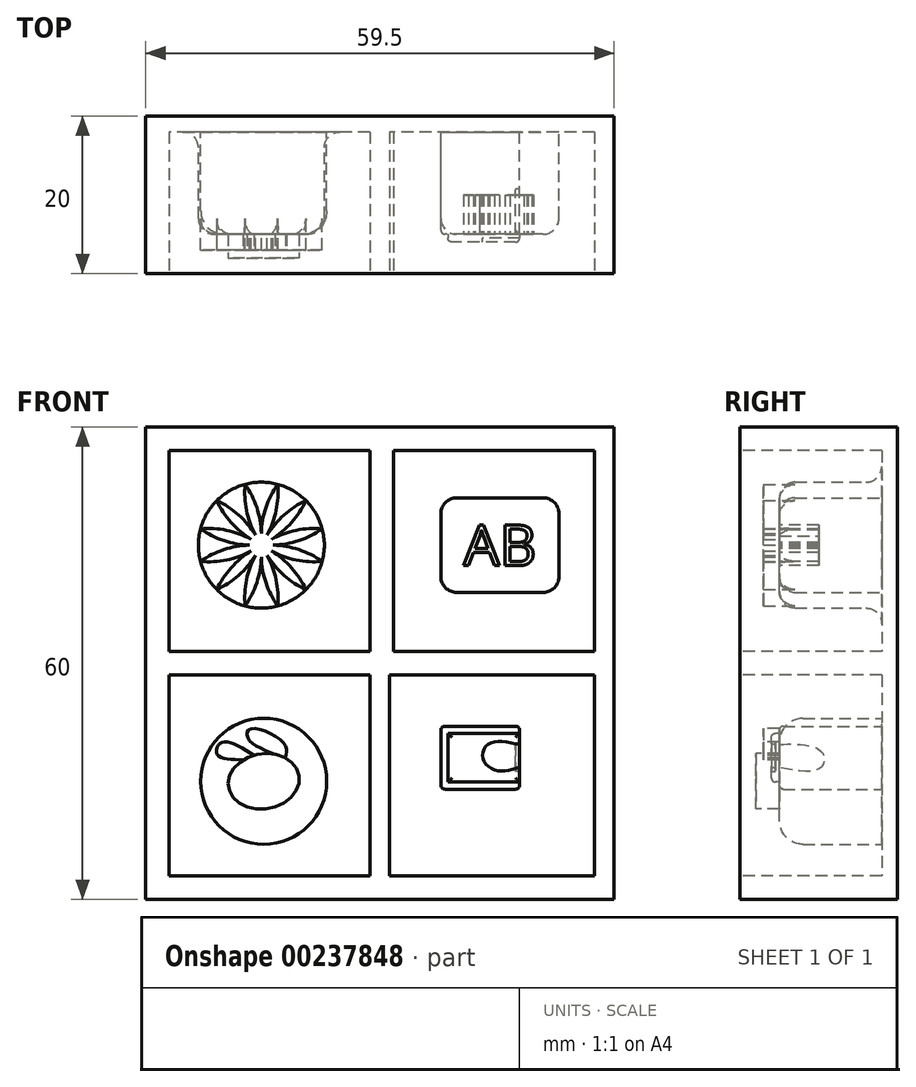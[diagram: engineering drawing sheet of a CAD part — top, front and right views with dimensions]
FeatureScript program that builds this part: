
annotation { "Feature Type Name" : "Feature", "Feature Type Description" : "" }
export const myFeature = defineFeature(function(context is Context, id is Id, definition is map)
    precondition{}
    {
        {
            var Q0;
            Q0=qCreatedBy(makeId("Front.planeOp"),FACE);
            var sketch = newSketch(context, id + "F0", { "sketchPlane" : qUnion([Q0])});
            skLineSegment(sketch, "E0.bottom", {"start": v(30, -30) * mm, "end": v(-30, -30) * mm});
            skLineSegment(sketch, "E0.top", {"start": v(30, 30) * mm, "end": v(-30, 30) * mm});
            skLineSegment(sketch, "E0.left", {"start": v(30, -30) * mm, "end": v(30, 30) * mm});
            skLineSegment(sketch, "E0.right", {"start": v(-30, -30) * mm, "end": v(-30, 30) * mm});
            skPoint(sketch, "E0.middle", {"position": v(0, 0) * mm});
            skSolve(sketch);
        }
        {
            var Q0;
            Q0 = qSketchRegion(id + "F2", true);
            var Q1;
            Q1=makeQuery(id+"F0.imprint","IMPRINT",FACE,{"disambiguationData":[TD([[makeQuery(id+"F0.imprint","IMPRINT",EDGE,{"derivedFrom":sQuery(id+"F0.wireOp",EDGE,"E0.bottom")}),-1.0]])]});
            var Q2;
            Q2 = qSketchRegion(id + "F6", true);
            extrude(context, id + "F1", {"entities" : qUnion([Q0, Q1, Q2]), "depth" : 20 * mm});
        }
        {
            var Q0;
            Q0=makeQuery(id+"F1.opExtrude","CAP_FACE",FACE,{"disambiguationData":[OSD([sQuery(id+"F0.wireOp",EDGE,"E0.bottom"),sQuery(id+"F0.wireOp",EDGE,"E0.top"),sQuery(id+"F0.wireOp",EDGE,"E0.left"),sQuery(id+"F0.wireOp",EDGE,"E0.right")])],"isStart":false});
            var sketch = newSketch(context, id + "F2", { "sketchPlane" : qUnion([Q0])});
            skLineSegment(sketch, "E1.bottom", {"start": v(27, 27) * mm, "end": v(-27, 27) * mm});
            skLineSegment(sketch, "E1.top", {"start": v(27, -27) * mm, "end": v(-27, -27) * mm});
            skLineSegment(sketch, "E1.left", {"start": v(27, 27) * mm, "end": v(27, -27) * mm});
            skLineSegment(sketch, "E1.right", {"start": v(-27, 27) * mm, "end": v(-27, -27) * mm});
            skPoint(sketch, "E1.middle", {"position": v(0, 0) * mm});
            skLineSegment(sketch, "E2.bottom", {"start": v(1.5, 27) * mm, "end": v(-1.5, 27) * mm});
            skLineSegment(sketch, "E2.top", {"start": v(1.5, -27) * mm, "end": v(-1.5, -27) * mm});
            skLineSegment(sketch, "E2.left", {"start": v(1.5, 27) * mm, "end": v(1.5, -27) * mm});
            skLineSegment(sketch, "E2.right", {"start": v(-1.5, 27) * mm, "end": v(-1.5, -27) * mm});
            skLineSegment(sketch, "E3.bottom", {"start": v(-27, 1.5) * mm, "end": v(27, 1.5) * mm});
            skLineSegment(sketch, "E3.top", {"start": v(-27, -1.5) * mm, "end": v(27, -1.5) * mm});
            skLineSegment(sketch, "E3.left", {"start": v(-27, 1.5) * mm, "end": v(-27, -1.5) * mm});
            skLineSegment(sketch, "E3.right", {"start": v(27, 1.5) * mm, "end": v(27, -1.5) * mm});
            skSolve(sketch);
        }
        {
            var Q0;
            {var subQ0=sQuery(id+"F2.wireOp",EDGE,"E1.right");var subQ1=sQuery(id+"F2.wireOp",EDGE,"E1.top");var subQ2=makeQuery(id+"F2.imprint","INTERSECT",VERTEX,{"derivedFrom":[subQ1,subQ0]});Q0=makeQuery(id+"F2.imprint","IMPRINT",FACE,{"disambiguationData":[TD([[makeQuery(id+"F2.imprint","IMPRINT",EDGE,{"disambiguationData":[TD([[subQ2,1.0]])],"derivedFrom":subQ1}),-1.0]])]});}
            extrude(context, id + "F3", {"entities" : qUnion([Q0]), "operationType" : NewBodyOperationType.REMOVE, "oppositeDirection" : true, "depth" : 18 * mm});
        }
        {
            var Q0;
            {var subQ0=sQuery(id+"F2.wireOp",EDGE,"E1.right");var subQ1=sQuery(id+"F2.wireOp",EDGE,"E1.bottom");var subQ2=makeQuery(id+"F2.imprint","INTERSECT",VERTEX,{"derivedFrom":[subQ1,subQ0]});Q0=makeQuery(id+"F2.imprint","IMPRINT",FACE,{"disambiguationData":[TD([[makeQuery(id+"F2.imprint","IMPRINT",EDGE,{"disambiguationData":[TD([[subQ2,1.0]])],"derivedFrom":subQ1}),1.0]])]});}
            extrude(context, id + "F4", {"entities" : qUnion([Q0]), "operationType" : NewBodyOperationType.REMOVE, "oppositeDirection" : true, "depth" : 18 * mm});
        }
        {
            var Q0;
            {var subQ0=sQuery(id+"F2.wireOp",EDGE,"E1.left");var subQ1=sQuery(id+"F2.wireOp",EDGE,"E1.top");var subQ2=makeQuery(id+"F2.imprint","INTERSECT",VERTEX,{"derivedFrom":[subQ1,subQ0]});Q0=makeQuery(id+"F2.imprint","IMPRINT",FACE,{"disambiguationData":[TD([[makeQuery(id+"F2.imprint","IMPRINT",EDGE,{"disambiguationData":[TD([[subQ2,-1.0]])],"derivedFrom":subQ1}),-1.0]])]});}
            var Q1;
            {var subQ0=sQuery(id+"F2.wireOp",EDGE,"E1.left");var subQ1=sQuery(id+"F2.wireOp",EDGE,"E1.bottom");var subQ2=makeQuery(id+"F2.imprint","INTERSECT",VERTEX,{"derivedFrom":[subQ1,subQ0]});Q1=makeQuery(id+"F2.imprint","IMPRINT",FACE,{"disambiguationData":[TD([[makeQuery(id+"F2.imprint","IMPRINT",EDGE,{"disambiguationData":[TD([[subQ2,-1.0]])],"derivedFrom":subQ1}),1.0]])]});}
            extrude(context, id + "F5", {"entities" : qUnion([Q0, Q1]), "operationType" : NewBodyOperationType.REMOVE, "oppositeDirection" : true, "depth" : 18 * mm});
        }
        {
            var Q0;
            Q0=qCreatedBy(makeId("Front.planeOp"),FACE);
            var sketch = newSketch(context, id + "F6", { "sketchPlane" : qUnion([Q0])});
            skCircle(sketch, "E4", {"center": v(-15.3, 15) * mm, "radius": 8 * mm});
            skCircle(sketch, "E5", {"center": v(-15, -15) * mm, "radius": 8 * mm});
            skLineSegment(sketch, "E6.bottom", {"start": v(22.5, 9) * mm, "end": v(7.5, 9) * mm});
            skLineSegment(sketch, "E6.top", {"start": v(22.5, 21) * mm, "end": v(7.5, 21) * mm});
            skLineSegment(sketch, "E6.left", {"start": v(22.5, 9) * mm, "end": v(22.5, 21) * mm});
            skLineSegment(sketch, "E6.right", {"start": v(7.5, 9) * mm, "end": v(7.5, 21) * mm});
            skPoint(sketch, "E6.middle", {"position": v(15, 15) * mm});
            skLineSegment(sketch, "E7.bottom", {"start": v(17.5, -16) * mm, "end": v(7.5, -16) * mm});
            skLineSegment(sketch, "E7.top", {"start": v(17.5, -8) * mm, "end": v(7.5, -8) * mm});
            skLineSegment(sketch, "E7.left", {"start": v(17.5, -16) * mm, "end": v(17.5, -8) * mm});
            skLineSegment(sketch, "E7.right", {"start": v(7.5, -16) * mm, "end": v(7.5, -8) * mm});
            skPoint(sketch, "E7.middle", {"position": v(12.5, -12) * mm});
            skSolve(sketch);
        }
        {
            var Q0;
            Q0=makeQuery(id+"F6.imprint","IMPRINT",FACE,{"disambiguationData":[TD([[makeQuery(id+"F6.imprint","IMPRINT",EDGE,{"derivedFrom":sQuery(id+"F6.wireOp",EDGE,"E4")}),1.0]])]});
            var Q1;
            Q1=makeQuery(id+"F6.imprint","IMPRINT",FACE,{"disambiguationData":[TD([[makeQuery(id+"F6.imprint","IMPRINT",EDGE,{"derivedFrom":sQuery(id+"F6.wireOp",EDGE,"E6.bottom")}),-1.0]])]});
            var Q2;
            Q2=makeQuery(id+"F6.imprint","IMPRINT",FACE,{"disambiguationData":[TD([[makeQuery(id+"F6.imprint","IMPRINT",EDGE,{"derivedFrom":sQuery(id+"F6.wireOp",EDGE,"E7.bottom")}),-1.0]])]});
            extrude(context, id + "F7", {"entities" : qUnion([Q0, Q1, Q2]), "operationType" : NewBodyOperationType.ADD, "depth" : 15 * mm});
        }
        {
            var Q0;
            Q0=makeQuery(id+"F6.imprint","IMPRINT",FACE,{"disambiguationData":[TD([[makeQuery(id+"F6.imprint","IMPRINT",EDGE,{"derivedFrom":sQuery(id+"F6.wireOp",EDGE,"E5")}),1.0]])]});
            var Q1;
            Q1=sQuery(id+"F6.wireOp",EDGE,"E5");
            extrude(context, id + "F8", {"entities" : qUnion([Q0]), "operationType" : NewBodyOperationType.ADD, "surfaceEntities" : qUnion([Q1]), "depth" : 15 * mm});
        }
        {
            var Q0;
            Q0=qCreatedBy(makeId("Front.planeOp"),FACE);
            var sketch = newSketch(context, id + "F9", { "sketchPlane" : qUnion([Q0])});
            skCircle(sketch, "E8", {"center": v(-15.3, 15) * mm, "radius": 1.5 * mm});
            skArc(sketch, "E9", {"start": v(-13.24, 7.27) * mm, "mid": v(-13.42, 10.58) * mm, "end": v(-14.56, 13.7) * mm});
            skArc(sketch, "E10.MirrorCS", {"start": v(-13.24, 7.27) * mm, "mid": v(-14.73, 10.23) * mm, "end": v(-15.3, 13.5) * mm});
            skArc(sketch, "E11.MirrorCS", {"start": v(-9.65, 9.34) * mm, "mid": v(-12.42, 11.16) * mm, "end": v(-14.56, 13.7) * mm});
            skArc(sketch, "E12.MirrorCS", {"start": v(-9.65, 9.34) * mm, "mid": v(-11.47, 12.12) * mm, "end": v(-14, 14.25) * mm});
            skArc(sketch, "E13.MirrorCS", {"start": v(-7.58, 12.93) * mm, "mid": v(-10.9, 13.11) * mm, "end": v(-14, 14.25) * mm});
            skArc(sketch, "E14.MirrorCS", {"start": v(-7.58, 12.93) * mm, "mid": v(-10.54, 14.43) * mm, "end": v(-13.8, 15) * mm});
            skArc(sketch, "E15.MirrorCS", {"start": v(-7.58, 17.07) * mm, "mid": v(-10.54, 15.57) * mm, "end": v(-13.8, 15) * mm});
            skArc(sketch, "E16.MirrorCS", {"start": v(-7.58, 17.07) * mm, "mid": v(-10.9, 16.89) * mm, "end": v(-14, 15.75) * mm});
            skArc(sketch, "E17.MirrorCS", {"start": v(-9.65, 20.66) * mm, "mid": v(-11.47, 17.88) * mm, "end": v(-14, 15.75) * mm});
            skArc(sketch, "E18.MirrorCS", {"start": v(-9.65, 20.66) * mm, "mid": v(-12.42, 18.84) * mm, "end": v(-14.56, 16.3) * mm});
            skArc(sketch, "E19.MirrorCS", {"start": v(-13.24, 22.73) * mm, "mid": v(-13.42, 19.42) * mm, "end": v(-14.56, 16.3) * mm});
            skArc(sketch, "E20.MirrorCS", {"start": v(-13.24, 22.73) * mm, "mid": v(-14.73, 19.77) * mm, "end": v(-15.3, 16.5) * mm});
            skArc(sketch, "E21.MirrorCS", {"start": v(-17.38, 22.73) * mm, "mid": v(-15.88, 19.77) * mm, "end": v(-15.3, 16.5) * mm});
            skArc(sketch, "E22.MirrorCS", {"start": v(-17.38, 22.73) * mm, "mid": v(-17.2, 19.42) * mm, "end": v(-16.06, 16.3) * mm});
            skArc(sketch, "E23.MirrorCS", {"start": v(-20.96, 20.66) * mm, "mid": v(-18.19, 18.84) * mm, "end": v(-16.06, 16.3) * mm});
            skArc(sketch, "E24.MirrorCS", {"start": v(-20.96, 20.66) * mm, "mid": v(-19.15, 17.88) * mm, "end": v(-16.6, 15.75) * mm});
            skArc(sketch, "E25.MirrorCS", {"start": v(-23.03, 17.07) * mm, "mid": v(-19.72, 16.89) * mm, "end": v(-16.6, 15.75) * mm});
            skArc(sketch, "E26.MirrorCS", {"start": v(-23.03, 17.07) * mm, "mid": v(-20.07, 15.57) * mm, "end": v(-16.8, 15) * mm});
            skArc(sketch, "E27.MirrorCS", {"start": v(-23.03, 12.93) * mm, "mid": v(-20.07, 14.43) * mm, "end": v(-16.8, 15) * mm});
            skArc(sketch, "E28.MirrorCS", {"start": v(-23.03, 12.93) * mm, "mid": v(-19.72, 13.11) * mm, "end": v(-16.6, 14.25) * mm});
            skArc(sketch, "E29.MirrorCS", {"start": v(-20.96, 9.34) * mm, "mid": v(-19.15, 12.12) * mm, "end": v(-16.6, 14.25) * mm});
            skArc(sketch, "E30.MirrorCS", {"start": v(-20.96, 9.34) * mm, "mid": v(-18.19, 11.16) * mm, "end": v(-16.06, 13.7) * mm});
            skArc(sketch, "E31.MirrorCS", {"start": v(-17.38, 7.27) * mm, "mid": v(-17.2, 10.58) * mm, "end": v(-16.06, 13.7) * mm});
            skArc(sketch, "E32.MirrorCS", {"start": v(-17.38, 7.27) * mm, "mid": v(-15.88, 10.23) * mm, "end": v(-15.3, 13.5) * mm});
            skSolve(sketch);
        }
        {
            var Q0;
            Q0 = qSketchRegion(id + "F9", true);
            extrude(context, id + "F10", {"entities" : qUnion([Q0]), "operationType" : NewBodyOperationType.ADD, "depth" : 17 * mm, "hasSecondDirection" : true, "secondDirectionOppositeDirection" : false, "secondDirectionDepth" : 2 * mm});
        }
        {
            var Q0;
            {var subQ0=sQuery(id+"F6.wireOp",EDGE,"E4");Q0=makeQuery(id+"F10.boolean.opBoolean","SPLIT",EDGE,{"disambiguationData":[TD([makeQuery(id+"F7.opExtrude","SWEPT_FACE",FACE,{"disambiguationData":[OSD([subQ0])]}),makeQuery(id+"F7.opExtrude","CAP_FACE",FACE,{"disambiguationData":[OSD([subQ0])],"isStart":false}),makeQuery(id+"F10.opExtrude","SWEPT_FACE",FACE,{"disambiguationData":[OSD([sQuery(id+"F9.wireOp",EDGE,"E17.MirrorCS")])]}),makeQuery(id+"F10.opExtrude","SWEPT_FACE",FACE,{"disambiguationData":[OSD([sQuery(id+"F9.wireOp",EDGE,"E18.MirrorCS")])]}),makeQuery(id+"F10.opExtrude","SWEPT_FACE",FACE,{"disambiguationData":[OSD([sQuery(id+"F9.wireOp",EDGE,"E19.MirrorCS")])]}),makeQuery(id+"F10.opExtrude","SWEPT_FACE",FACE,{"disambiguationData":[OSD([sQuery(id+"F9.wireOp",EDGE,"E20.MirrorCS")])]})])],"derivedFrom":makeQuery(id+"F7.opExtrude","CAP_EDGE",EDGE,{"disambiguationData":[OSD([subQ0])],"isStart":false})});}
            var Q1;
            {var subQ0=sQuery(id+"F6.wireOp",EDGE,"E4");Q1=makeQuery(id+"F10.boolean.opBoolean","SPLIT",EDGE,{"disambiguationData":[TD([makeQuery(id+"F7.opExtrude","SWEPT_FACE",FACE,{"disambiguationData":[OSD([subQ0])]}),makeQuery(id+"F7.opExtrude","CAP_FACE",FACE,{"disambiguationData":[OSD([subQ0])],"isStart":false}),makeQuery(id+"F10.opExtrude","SWEPT_FACE",FACE,{"disambiguationData":[OSD([sQuery(id+"F9.wireOp",EDGE,"E19.MirrorCS")])]}),makeQuery(id+"F10.opExtrude","SWEPT_FACE",FACE,{"disambiguationData":[OSD([sQuery(id+"F9.wireOp",EDGE,"E20.MirrorCS")])]}),makeQuery(id+"F10.opExtrude","SWEPT_FACE",FACE,{"disambiguationData":[OSD([sQuery(id+"F9.wireOp",EDGE,"E21.MirrorCS")])]}),makeQuery(id+"F10.opExtrude","SWEPT_FACE",FACE,{"disambiguationData":[OSD([sQuery(id+"F9.wireOp",EDGE,"E22.MirrorCS")])]})])],"derivedFrom":makeQuery(id+"F7.opExtrude","CAP_EDGE",EDGE,{"disambiguationData":[OSD([subQ0])],"isStart":false})});}
            var Q2;
            {var subQ0=sQuery(id+"F6.wireOp",EDGE,"E4");Q2=makeQuery(id+"F10.boolean.opBoolean","SPLIT",EDGE,{"disambiguationData":[TD([makeQuery(id+"F7.opExtrude","SWEPT_FACE",FACE,{"disambiguationData":[OSD([subQ0])]}),makeQuery(id+"F7.opExtrude","CAP_FACE",FACE,{"disambiguationData":[OSD([subQ0])],"isStart":false}),makeQuery(id+"F10.opExtrude","SWEPT_FACE",FACE,{"disambiguationData":[OSD([sQuery(id+"F9.wireOp",EDGE,"E21.MirrorCS")])]}),makeQuery(id+"F10.opExtrude","SWEPT_FACE",FACE,{"disambiguationData":[OSD([sQuery(id+"F9.wireOp",EDGE,"E22.MirrorCS")])]}),makeQuery(id+"F10.opExtrude","SWEPT_FACE",FACE,{"disambiguationData":[OSD([sQuery(id+"F9.wireOp",EDGE,"E23.MirrorCS")])]}),makeQuery(id+"F10.opExtrude","SWEPT_FACE",FACE,{"disambiguationData":[OSD([sQuery(id+"F9.wireOp",EDGE,"E24.MirrorCS")])]})])],"derivedFrom":makeQuery(id+"F7.opExtrude","CAP_EDGE",EDGE,{"disambiguationData":[OSD([subQ0])],"isStart":false})});}
            var Q3;
            {var subQ0=sQuery(id+"F6.wireOp",EDGE,"E4");Q3=makeQuery(id+"F10.boolean.opBoolean","SPLIT",EDGE,{"disambiguationData":[TD([makeQuery(id+"F7.opExtrude","SWEPT_FACE",FACE,{"disambiguationData":[OSD([subQ0])]}),makeQuery(id+"F7.opExtrude","CAP_FACE",FACE,{"disambiguationData":[OSD([subQ0])],"isStart":false}),makeQuery(id+"F10.opExtrude","SWEPT_FACE",FACE,{"disambiguationData":[OSD([sQuery(id+"F9.wireOp",EDGE,"E23.MirrorCS")])]}),makeQuery(id+"F10.opExtrude","SWEPT_FACE",FACE,{"disambiguationData":[OSD([sQuery(id+"F9.wireOp",EDGE,"E24.MirrorCS")])]}),makeQuery(id+"F10.opExtrude","SWEPT_FACE",FACE,{"disambiguationData":[OSD([sQuery(id+"F9.wireOp",EDGE,"E25.MirrorCS")])]}),makeQuery(id+"F10.opExtrude","SWEPT_FACE",FACE,{"disambiguationData":[OSD([sQuery(id+"F9.wireOp",EDGE,"E26.MirrorCS")])]})])],"derivedFrom":makeQuery(id+"F7.opExtrude","CAP_EDGE",EDGE,{"disambiguationData":[OSD([subQ0])],"isStart":false})});}
            var Q4;
            {var subQ0=sQuery(id+"F6.wireOp",EDGE,"E4");Q4=makeQuery(id+"F10.boolean.opBoolean","SPLIT",EDGE,{"disambiguationData":[TD([makeQuery(id+"F7.opExtrude","SWEPT_FACE",FACE,{"disambiguationData":[OSD([subQ0])]}),makeQuery(id+"F7.opExtrude","CAP_FACE",FACE,{"disambiguationData":[OSD([subQ0])],"isStart":false}),makeQuery(id+"F10.opExtrude","SWEPT_FACE",FACE,{"disambiguationData":[OSD([sQuery(id+"F9.wireOp",EDGE,"E25.MirrorCS")])]}),makeQuery(id+"F10.opExtrude","SWEPT_FACE",FACE,{"disambiguationData":[OSD([sQuery(id+"F9.wireOp",EDGE,"E26.MirrorCS")])]}),makeQuery(id+"F10.opExtrude","SWEPT_FACE",FACE,{"disambiguationData":[OSD([sQuery(id+"F9.wireOp",EDGE,"E27.MirrorCS")])]}),makeQuery(id+"F10.opExtrude","SWEPT_FACE",FACE,{"disambiguationData":[OSD([sQuery(id+"F9.wireOp",EDGE,"E28.MirrorCS")])]})])],"derivedFrom":makeQuery(id+"F7.opExtrude","CAP_EDGE",EDGE,{"disambiguationData":[OSD([subQ0])],"isStart":false})});}
            var Q5;
            {var subQ0=sQuery(id+"F6.wireOp",EDGE,"E4");Q5=makeQuery(id+"F10.boolean.opBoolean","SPLIT",EDGE,{"disambiguationData":[TD([makeQuery(id+"F7.opExtrude","SWEPT_FACE",FACE,{"disambiguationData":[OSD([subQ0])]}),makeQuery(id+"F7.opExtrude","CAP_FACE",FACE,{"disambiguationData":[OSD([subQ0])],"isStart":false}),makeQuery(id+"F10.opExtrude","SWEPT_FACE",FACE,{"disambiguationData":[OSD([sQuery(id+"F9.wireOp",EDGE,"E27.MirrorCS")])]}),makeQuery(id+"F10.opExtrude","SWEPT_FACE",FACE,{"disambiguationData":[OSD([sQuery(id+"F9.wireOp",EDGE,"E28.MirrorCS")])]}),makeQuery(id+"F10.opExtrude","SWEPT_FACE",FACE,{"disambiguationData":[OSD([sQuery(id+"F9.wireOp",EDGE,"E29.MirrorCS")])]}),makeQuery(id+"F10.opExtrude","SWEPT_FACE",FACE,{"disambiguationData":[OSD([sQuery(id+"F9.wireOp",EDGE,"E30.MirrorCS")])]})])],"derivedFrom":makeQuery(id+"F7.opExtrude","CAP_EDGE",EDGE,{"disambiguationData":[OSD([subQ0])],"isStart":false})});}
            var Q6;
            {var subQ0=sQuery(id+"F6.wireOp",EDGE,"E4");Q6=makeQuery(id+"F10.boolean.opBoolean","SPLIT",EDGE,{"disambiguationData":[TD([makeQuery(id+"F7.opExtrude","SWEPT_FACE",FACE,{"disambiguationData":[OSD([subQ0])]}),makeQuery(id+"F7.opExtrude","CAP_FACE",FACE,{"disambiguationData":[OSD([subQ0])],"isStart":false}),makeQuery(id+"F10.opExtrude","SWEPT_FACE",FACE,{"disambiguationData":[OSD([sQuery(id+"F9.wireOp",EDGE,"E29.MirrorCS")])]}),makeQuery(id+"F10.opExtrude","SWEPT_FACE",FACE,{"disambiguationData":[OSD([sQuery(id+"F9.wireOp",EDGE,"E30.MirrorCS")])]}),makeQuery(id+"F10.opExtrude","SWEPT_FACE",FACE,{"disambiguationData":[OSD([sQuery(id+"F9.wireOp",EDGE,"E31.MirrorCS")])]}),makeQuery(id+"F10.opExtrude","SWEPT_FACE",FACE,{"disambiguationData":[OSD([sQuery(id+"F9.wireOp",EDGE,"E32.MirrorCS")])]})])],"derivedFrom":makeQuery(id+"F7.opExtrude","CAP_EDGE",EDGE,{"disambiguationData":[OSD([subQ0])],"isStart":false})});}
            var Q7;
            {var subQ0=sQuery(id+"F6.wireOp",EDGE,"E4");Q7=makeQuery(id+"F10.boolean.opBoolean","SPLIT",EDGE,{"disambiguationData":[TD([makeQuery(id+"F7.opExtrude","SWEPT_FACE",FACE,{"disambiguationData":[OSD([subQ0])]}),makeQuery(id+"F7.opExtrude","CAP_FACE",FACE,{"disambiguationData":[OSD([subQ0])],"isStart":false}),makeQuery(id+"F10.opExtrude","SWEPT_FACE",FACE,{"disambiguationData":[OSD([sQuery(id+"F9.wireOp",EDGE,"E10.MirrorCS")])]}),makeQuery(id+"F10.opExtrude","SWEPT_FACE",FACE,{"disambiguationData":[OSD([sQuery(id+"F9.wireOp",EDGE,"E9")])]}),makeQuery(id+"F10.opExtrude","SWEPT_FACE",FACE,{"disambiguationData":[OSD([sQuery(id+"F9.wireOp",EDGE,"E31.MirrorCS")])]}),makeQuery(id+"F10.opExtrude","SWEPT_FACE",FACE,{"disambiguationData":[OSD([sQuery(id+"F9.wireOp",EDGE,"E32.MirrorCS")])]})])],"derivedFrom":makeQuery(id+"F7.opExtrude","CAP_EDGE",EDGE,{"disambiguationData":[OSD([subQ0])],"isStart":false})});}
            var Q8;
            {var subQ0=sQuery(id+"F6.wireOp",EDGE,"E4");Q8=makeQuery(id+"F10.boolean.opBoolean","SPLIT",EDGE,{"disambiguationData":[TD([makeQuery(id+"F7.opExtrude","SWEPT_FACE",FACE,{"disambiguationData":[OSD([subQ0])]}),makeQuery(id+"F7.opExtrude","CAP_FACE",FACE,{"disambiguationData":[OSD([subQ0])],"isStart":false}),makeQuery(id+"F10.opExtrude","SWEPT_FACE",FACE,{"disambiguationData":[OSD([sQuery(id+"F9.wireOp",EDGE,"E11.MirrorCS")])]}),makeQuery(id+"F10.opExtrude","SWEPT_FACE",FACE,{"disambiguationData":[OSD([sQuery(id+"F9.wireOp",EDGE,"E10.MirrorCS")])]}),makeQuery(id+"F10.opExtrude","SWEPT_FACE",FACE,{"disambiguationData":[OSD([sQuery(id+"F9.wireOp",EDGE,"E12.MirrorCS")])]}),makeQuery(id+"F10.opExtrude","SWEPT_FACE",FACE,{"disambiguationData":[OSD([sQuery(id+"F9.wireOp",EDGE,"E9")])]})])],"derivedFrom":makeQuery(id+"F7.opExtrude","CAP_EDGE",EDGE,{"disambiguationData":[OSD([subQ0])],"isStart":false})});}
            var Q9;
            {var subQ0=sQuery(id+"F6.wireOp",EDGE,"E4");Q9=makeQuery(id+"F10.boolean.opBoolean","SPLIT",EDGE,{"disambiguationData":[TD([makeQuery(id+"F7.opExtrude","SWEPT_FACE",FACE,{"disambiguationData":[OSD([subQ0])]}),makeQuery(id+"F7.opExtrude","CAP_FACE",FACE,{"disambiguationData":[OSD([subQ0])],"isStart":false}),makeQuery(id+"F10.opExtrude","SWEPT_FACE",FACE,{"disambiguationData":[OSD([sQuery(id+"F9.wireOp",EDGE,"E11.MirrorCS")])]}),makeQuery(id+"F10.opExtrude","SWEPT_FACE",FACE,{"disambiguationData":[OSD([sQuery(id+"F9.wireOp",EDGE,"E12.MirrorCS")])]}),makeQuery(id+"F10.opExtrude","SWEPT_FACE",FACE,{"disambiguationData":[OSD([sQuery(id+"F9.wireOp",EDGE,"E13.MirrorCS")])]}),makeQuery(id+"F10.opExtrude","SWEPT_FACE",FACE,{"disambiguationData":[OSD([sQuery(id+"F9.wireOp",EDGE,"E14.MirrorCS")])]})])],"derivedFrom":makeQuery(id+"F7.opExtrude","CAP_EDGE",EDGE,{"disambiguationData":[OSD([subQ0])],"isStart":false})});}
            var Q10;
            Q10=makeQuery(id+"F7.boolean.opBoolean","INTERSECT",EDGE,{"derivedFrom":[makeQuery(id+"F4.boolean.opBoolean","COPY",FACE,{"derivedFrom":makeQuery(id+"F4.opExtrude","CAP_FACE",FACE,{"disambiguationData":[OSD([sQuery(id+"F2.wireOp",EDGE,"E1.bottom"),sQuery(id+"F2.wireOp",EDGE,"E1.right"),sQuery(id+"F2.wireOp",EDGE,"E2.right"),sQuery(id+"F2.wireOp",EDGE,"E3.bottom")])],"isStart":false})}),makeQuery(id+"F7.opExtrude","SWEPT_FACE",FACE,{"disambiguationData":[OSD([sQuery(id+"F6.wireOp",EDGE,"E4")])]})]});
            var Q11;
            {var subQ0=sQuery(id+"F6.wireOp",EDGE,"E4");Q11=makeQuery(id+"F10.boolean.opBoolean","SPLIT",EDGE,{"disambiguationData":[TD([makeQuery(id+"F7.opExtrude","SWEPT_FACE",FACE,{"disambiguationData":[OSD([subQ0])]}),makeQuery(id+"F7.opExtrude","CAP_FACE",FACE,{"disambiguationData":[OSD([subQ0])],"isStart":false}),makeQuery(id+"F10.opExtrude","SWEPT_FACE",FACE,{"disambiguationData":[OSD([sQuery(id+"F9.wireOp",EDGE,"E15.MirrorCS")])]}),makeQuery(id+"F10.opExtrude","SWEPT_FACE",FACE,{"disambiguationData":[OSD([sQuery(id+"F9.wireOp",EDGE,"E16.MirrorCS")])]}),makeQuery(id+"F10.opExtrude","SWEPT_FACE",FACE,{"disambiguationData":[OSD([sQuery(id+"F9.wireOp",EDGE,"E17.MirrorCS")])]}),makeQuery(id+"F10.opExtrude","SWEPT_FACE",FACE,{"disambiguationData":[OSD([sQuery(id+"F9.wireOp",EDGE,"E18.MirrorCS")])]})])],"derivedFrom":makeQuery(id+"F7.opExtrude","CAP_EDGE",EDGE,{"disambiguationData":[OSD([subQ0])],"isStart":false})});}
            fillet(context, id + "F11", {"entities" : qUnion([Q0, Q1, Q2, Q3, Q4, Q5, Q6, Q7, Q8, Q9, Q10, Q11]), "radius" : 2 * mm, "tangentPropagation" : true, "allowEdgeOverflow" : false});
        }
        {
            var Q0;
            {var subQ0=sQuery(id+"F2.wireOp",EDGE,"E1.right");var subQ1=sQuery(id+"F2.wireOp",EDGE,"E1.top");var subQ2=makeQuery(id+"F2.imprint","INTERSECT",VERTEX,{"derivedFrom":[subQ1,subQ0]});Q0=makeQuery(id+"F2.imprint","IMPRINT",FACE,{"disambiguationData":[TD([[makeQuery(id+"F2.imprint","IMPRINT",EDGE,{"disambiguationData":[TD([[subQ2,1.0]])],"derivedFrom":subQ1}),-1.0]])]});}
            var sketch = newSketch(context, id + "F12", { "sketchPlane" : qUnion([Q0])});
            skEllipse(sketch, "E33", {"center": v(-15, -15) * mm, "majorRadius": 4.53 * mm, "minorRadius": 3.5 * mm, "majorAxis": v(0.99, 0.16)});
            skFitSpline(sketch, "E34", {"points": [v(-17.6, -12.3) * mm, v(-20.93, -11.53) * mm, v(-20.39, -10.07) * mm, v(-16.23, -11.7) * mm], "startDerivative": vector(-12.55, 0.37) * mm, "endDerivative": vector(12.08, -7.5) * mm});
            skFitSpline(sketch, "E35", {"points": [v(-13.55, -11.58) * mm, v(-17.02, -9.52) * mm, v(-16.66, -8.34) * mm, v(-12.38, -10.25) * mm, v(-12.26, -12.03) * mm], "startDerivative": vector(-15.02, 5.93) * mm, "endDerivative": vector(-2.63, -8.47) * mm});
            skArc(sketch, "E36", {"start": v(-16.02, -14.16) * mm, "mid": v(-17.23, -13.72) * mm, "end": v(-17.93, -14.8) * mm});
            skArc(sketch, "E37", {"start": v(-12.56, -13.25) * mm, "mid": v(-13.6, -12.58) * mm, "end": v(-14.3, -13.62) * mm});
            skArc(sketch, "E38", {"start": v(-16.23, -16.9) * mm, "mid": v(-14.3, -17.3) * mm, "end": v(-12.56, -16.35) * mm});
            skSolve(sketch);
        }
        {
            var Q0;
            {var subQ0=sQuery(id+"F12.wireOp",EDGE,"E35");var subQ1=sQuery(id+"F12.wireOp",EDGE,"E33");var subQ2=makeQuery(id+"F12.imprint","INTERSECT",VERTEX,{"disambiguationData":[OD(0.0)],"derivedFrom":[subQ1,subQ0]});Q0=makeQuery(id+"F12.imprint","IMPRINT",FACE,{"disambiguationData":[TD([[makeQuery(id+"F12.imprint","IMPRINT",EDGE,{"disambiguationData":[TD([[subQ2,1.0]])],"derivedFrom":subQ1}),1.0]])]});}
            var Q1;
            Q1=sQuery(id+"F12.wireOp",EDGE,"E34");
            var Q2;
            Q2=sQuery(id+"F12.wireOp",EDGE,"E35");
            var Q3;
            Q3=sQuery(id+"F12.wireOp",EDGE,"E33");
            var Q4;
            Q4=sQuery(id+"F12.wireOp",EDGE,"E38");
            extrude(context, id + "F13", {"entities" : qUnion([Q0]), "surfaceEntities" : qUnion([Q1, Q2, Q3, Q4]), "oppositeDirection" : true, "depth" : 5 * mm, "hasSecondDirection" : true, "secondDirectionOppositeDirection" : true, "secondDirectionDepth" : 2 * mm});
        }
        {
            var Q0;
            {var subQ0=sQuery(id+"F12.wireOp",EDGE,"E35");Q0=makeQuery(id+"F12.imprint","IMPRINT",FACE,{"disambiguationData":[TD([[makeQuery(id+"F12.imprint","IMPRINT",EDGE,{"derivedFrom":subQ0}),-1.0]])]});}
            var Q1;
            {var subQ0=sQuery(id+"F12.wireOp",EDGE,"E34");Q1=makeQuery(id+"F12.imprint","IMPRINT",FACE,{"disambiguationData":[TD([[makeQuery(id+"F12.imprint","IMPRINT",EDGE,{"derivedFrom":subQ0}),-1.0]])]});}
            var Q2;
            Q2=sQuery(id+"F12.wireOp",EDGE,"E34");
            var Q3;
            Q3=sQuery(id+"F12.wireOp",EDGE,"E35");
            extrude(context, id + "F14", {"entities" : qUnion([Q0, Q1]), "surfaceEntities" : qUnion([Q2, Q3]), "oppositeDirection" : true, "depth" : 5 * mm, "hasSecondDirection" : true, "secondDirectionOppositeDirection" : true, "secondDirectionDepth" : 3 * mm});
        }
        {
            var Q0;
            Q0=makeQuery(id+"F8.opExtrude","CAP_EDGE",EDGE,{"disambiguationData":[OSD([sQuery(id+"F6.wireOp",EDGE,"E5")])],"isStart":false});
            fillet(context, id + "F15", {"entities" : qUnion([Q0]), "radius" : 3 * mm, "tangentPropagation" : true, "allowEdgeOverflow" : false});
        }
        {
            var Q0;
            {var subQ0=sQuery(id+"F2.wireOp",EDGE,"E1.left");var subQ1=sQuery(id+"F2.wireOp",EDGE,"E1.bottom");var subQ2=makeQuery(id+"F2.imprint","INTERSECT",VERTEX,{"derivedFrom":[subQ1,subQ0]});Q0=makeQuery(id+"F2.imprint","IMPRINT",FACE,{"disambiguationData":[TD([[makeQuery(id+"F2.imprint","IMPRINT",EDGE,{"disambiguationData":[TD([[subQ2,-1.0]])],"derivedFrom":subQ1}),1.0]])]});}
            var sketch = newSketch(context, id + "F16", { "sketchPlane" : qUnion([Q0])});
            skText(sketch, "E39", { "text": "AB\n", "fontName": "OpenSans-Regular.ttf"});
            const initialGuessF16  = {"E39": [0.01038, 0.0124, 1, 0, 0.0052]};
            skSetInitialGuess(sketch, initialGuessF16);
            skSolve(sketch);
        }
        {
            var Q0;
            Q0 = qSketchRegion(id + "F16", true);
            extrude(context, id + "F17", {"entities" : qUnion([Q0]), "operationType" : NewBodyOperationType.REMOVE, "oppositeDirection" : true, "depth" : 10 * mm});
        }
        {
            var Q0;
            Q0=makeQuery(id+"F7.opExtrude","SWEPT_EDGE",EDGE,{"disambiguationData":[OSD([sQuery(id+"F6.wireOp",EDGE,"E6.top"),sQuery(id+"F6.wireOp",EDGE,"E6.right")])]});
            var Q1;
            Q1=makeQuery(id+"F7.opExtrude","SWEPT_EDGE",EDGE,{"disambiguationData":[OSD([sQuery(id+"F6.wireOp",EDGE,"E6.top"),sQuery(id+"F6.wireOp",EDGE,"E6.left")])]});
            var Q2;
            Q2=makeQuery(id+"F7.opExtrude","SWEPT_EDGE",EDGE,{"disambiguationData":[OSD([sQuery(id+"F6.wireOp",EDGE,"E6.bottom"),sQuery(id+"F6.wireOp",EDGE,"E6.right")])]});
            var Q3;
            Q3=makeQuery(id+"F7.opExtrude","SWEPT_EDGE",EDGE,{"disambiguationData":[OSD([sQuery(id+"F6.wireOp",EDGE,"E6.bottom"),sQuery(id+"F6.wireOp",EDGE,"E6.left")])]});
            var Q4;
            Q4=makeQuery(id+"F7.opExtrude","CAP_EDGE",EDGE,{"disambiguationData":[OSD([sQuery(id+"F6.wireOp",EDGE,"E6.top")])],"isStart":false});
            var Q5;
            Q5=makeQuery(id+"F7.opExtrude","CAP_EDGE",EDGE,{"disambiguationData":[OSD([sQuery(id+"F6.wireOp",EDGE,"E6.bottom")])],"isStart":false});
            var Q6;
            Q6=makeQuery(id+"F7.opExtrude","CAP_EDGE",EDGE,{"disambiguationData":[OSD([sQuery(id+"F6.wireOp",EDGE,"E6.right")])],"isStart":false});
            var Q7;
            Q7=makeQuery(id+"F7.opExtrude","CAP_EDGE",EDGE,{"disambiguationData":[OSD([sQuery(id+"F6.wireOp",EDGE,"E6.left")])],"isStart":false});
            fillet(context, id + "F18", {"entities" : qUnion([Q0, Q1, Q2, Q3, Q4, Q5, Q6, Q7]), "radius" : 2 * mm, "tangentPropagation" : true, "allowEdgeOverflow" : false});
        }
        {
            var Q0;
            {var subQ0=sQuery(id+"F2.wireOp",EDGE,"E1.left");var subQ1=sQuery(id+"F2.wireOp",EDGE,"E1.top");var subQ2=makeQuery(id+"F2.imprint","INTERSECT",VERTEX,{"derivedFrom":[subQ1,subQ0]});Q0=makeQuery(id+"F2.imprint","IMPRINT",FACE,{"disambiguationData":[TD([[makeQuery(id+"F2.imprint","IMPRINT",EDGE,{"disambiguationData":[TD([[subQ2,-1.0]])],"derivedFrom":subQ1}),-1.0]])]});}
            var sketch = newSketch(context, id + "F19", { "sketchPlane" : qUnion([Q0])});
            skLineSegment(sketch, "E40.bottom", {"start": v(17.5, -15.1) * mm, "end": v(8.4, -15.1) * mm});
            skLineSegment(sketch, "E40.top", {"start": v(17.5, -8.9) * mm, "end": v(8.4, -8.9) * mm});
            skLineSegment(sketch, "E40.left", {"start": v(17.5, -15.1) * mm, "end": v(17.5, -8.9) * mm});
            skLineSegment(sketch, "E40.right", {"start": v(8.4, -15.1) * mm, "end": v(8.4, -8.9) * mm});
            skPoint(sketch, "E40.middle", {"position": v(12.95, -12) * mm});
            skSolve(sketch);
        }
        {
            var Q0;
            {var subQ0=sQuery(id+"F2.wireOp",EDGE,"E1.left");var subQ1=sQuery(id+"F2.wireOp",EDGE,"E1.top");var subQ2=makeQuery(id+"F2.imprint","INTERSECT",VERTEX,{"derivedFrom":[subQ1,subQ0]});Q0=makeQuery(id+"F2.imprint","IMPRINT",FACE,{"disambiguationData":[TD([[makeQuery(id+"F2.imprint","IMPRINT",EDGE,{"disambiguationData":[TD([[subQ2,-1.0]])],"derivedFrom":subQ1}),-1.0]])]});}
            var sketch = newSketch(context, id + "F20", { "sketchPlane" : qUnion([Q0])});
            skFitSpline(sketch, "E41", {"points": [v(17.5, -10.33) * mm, v(13.66, -10.2) * mm, v(12.82, -12.05) * mm, v(14.56, -13.63) * mm, v(17.5, -13.21) * mm], "startDerivative": vector(-14.94, 3.16) * mm, "endDerivative": vector(11.85, 3.75) * mm});
            skLineSegment(sketch, "E42", {"start": v(17.5, -13.21) * mm, "end": v(17.5, -10.33) * mm});
            skSolve(sketch);
        }
        {
            var Q0;
            Q0=makeQuery(id+"F19.imprint","IMPRINT",FACE,{"disambiguationData":[TD([[makeQuery(id+"F19.imprint","IMPRINT",EDGE,{"derivedFrom":sQuery(id+"F19.wireOp",EDGE,"E40.bottom")}),-1.0]])]});
            var Q1;
            Q1=sQuery(id+"F20.wireOp",EDGE,"E41");
            extrude(context, id + "F21", {"entities" : qUnion([Q0]), "surfaceEntities" : qUnion([Q1]), "oppositeDirection" : true, "depth" : 5 * mm, "hasSecondDirection" : true, "secondDirectionOppositeDirection" : true, "secondDirectionDepth" : 4 * mm});
        }
        {
            var Q0;
            Q0=makeQuery(id+"F20.imprint","IMPRINT",FACE,{"disambiguationData":[TD([[makeQuery(id+"F20.imprint","IMPRINT",EDGE,{"derivedFrom":sQuery(id+"F20.wireOp",EDGE,"E41")}),1.0]])]});
            var Q1;
            Q1=sQuery(id+"F20.wireOp",EDGE,"E41");
            extrude(context, id + "F22", {"entities" : qUnion([Q0]), "operationType" : NewBodyOperationType.REMOVE, "surfaceEntities" : qUnion([Q1]), "oppositeDirection" : true, "depth" : 4.5 * mm});
        }
        {
            var Q0;
            Q0=makeQuery(id+"F7.opExtrude","SWEPT_EDGE",EDGE,{"disambiguationData":[OSD([sQuery(id+"F6.wireOp",EDGE,"E7.top"),sQuery(id+"F6.wireOp",EDGE,"E7.right")])]});
            fillet(context, id + "F23", {"entities" : qUnion([Q0]), "radius" : 0.5 * mm, "tangentPropagation" : true, "allowEdgeOverflow" : false});
        }
        {
            var Q0;
            Q0=makeQuery(id+"F21.opExtrude","CAP_EDGE",EDGE,{"disambiguationData":[OSD([sQuery(id+"F19.wireOp",EDGE,"E40.right")])],"isStart":true});
            var Q1;
            Q1=makeQuery(id+"F21.opExtrude","CAP_EDGE",EDGE,{"disambiguationData":[OSD([sQuery(id+"F19.wireOp",EDGE,"E40.top")])],"isStart":true});
            var Q2;
            Q2=makeQuery(id+"F21.opExtrude","CAP_EDGE",EDGE,{"disambiguationData":[OSD([sQuery(id+"F19.wireOp",EDGE,"E40.bottom")])],"isStart":true});
            var Q3;
            {var subQ0=sQuery(id+"F19.wireOp",EDGE,"E40.bottom");var subQ1=sQuery(id+"F19.wireOp",EDGE,"E40.left");Q3=makeQuery(id+"F22.boolean.opBoolean","SPLIT",EDGE,{"disambiguationData":[TD([makeQuery(id+"F21.opExtrude","SWEPT_FACE",FACE,{"disambiguationData":[OSD([subQ0])]})])],"derivedFrom":makeQuery(id+"F21.opExtrude","CAP_EDGE",EDGE,{"disambiguationData":[OSD([subQ1])],"isStart":true})});}
            var Q4;
            {var subQ0=sQuery(id+"F19.wireOp",EDGE,"E40.left");var subQ1=sQuery(id+"F19.wireOp",EDGE,"E40.top");Q4=makeQuery(id+"F22.boolean.opBoolean","SPLIT",EDGE,{"disambiguationData":[TD([makeQuery(id+"F21.opExtrude","SWEPT_FACE",FACE,{"disambiguationData":[OSD([subQ1])]})])],"derivedFrom":makeQuery(id+"F21.opExtrude","CAP_EDGE",EDGE,{"disambiguationData":[OSD([subQ0])],"isStart":true})});}
            var Q5;
            Q5=makeQuery(id+"F7.opExtrude","CAP_EDGE",EDGE,{"disambiguationData":[OSD([sQuery(id+"F6.wireOp",EDGE,"E7.right")])],"isStart":false});
            var Q6;
            Q6=makeQuery(id+"F7.opExtrude","CAP_EDGE",EDGE,{"disambiguationData":[OSD([sQuery(id+"F6.wireOp",EDGE,"E7.bottom")])],"isStart":false});
            var Q7;
            Q7=makeQuery(id+"F7.opExtrude","SWEPT_EDGE",EDGE,{"disambiguationData":[OSD([sQuery(id+"F6.wireOp",EDGE,"E7.bottom"),sQuery(id+"F6.wireOp",EDGE,"E7.right")])]});
            var Q8;
            Q8=makeQuery(id+"F7.opExtrude","SWEPT_EDGE",EDGE,{"disambiguationData":[OSD([sQuery(id+"F6.wireOp",EDGE,"E7.bottom"),sQuery(id+"F6.wireOp",EDGE,"E7.left")])]});
            var Q9;
            Q9=makeQuery(id+"F7.opExtrude","SWEPT_EDGE",EDGE,{"disambiguationData":[OSD([sQuery(id+"F6.wireOp",EDGE,"E7.top"),sQuery(id+"F6.wireOp",EDGE,"E7.left")])]});
            var Q10;
            Q10=makeQuery(id+"F7.opExtrude","CAP_EDGE",EDGE,{"disambiguationData":[OSD([sQuery(id+"F6.wireOp",EDGE,"E7.top")])],"isStart":false});
            var Q11;
            {var subQ0=sQuery(id+"F6.wireOp",EDGE,"E7.top");Q11=makeQuery(id+"F23.opFillet","BLEND_EDGE",EDGE,{"blendedFrom":[makeQuery(id+"F7.opExtrude","SWEPT_EDGE",EDGE,{"disambiguationData":[OSD([subQ0,sQuery(id+"F6.wireOp",EDGE,"E7.right")])]}),makeQuery(id+"F7.opExtrude","SWEPT_FACE",FACE,{"disambiguationData":[OSD([subQ0])]})],"blendedInto":[makeQuery(id+"F7.opExtrude","SWEPT_FACE",FACE,{"disambiguationData":[OSD([subQ0])]})]});}
            fillet(context, id + "F24", {"entities" : qUnion([Q0, Q1, Q2, Q3, Q4, Q5, Q6, Q7, Q8, Q9, Q10, Q11]), "radius" : 0.5 * mm, "tangentPropagation" : true, "allowEdgeOverflow" : false});
        }
        {
            var Q0;
            Q0=makeQuery(id+"F7.opExtrude","SWEPT_FACE",FACE,{"disambiguationData":[OSD([sQuery(id+"F6.wireOp",EDGE,"E7.left")])]});
            var sketch = newSketch(context, id + "F25", { "sketchPlane" : qUnion([Q0])});
            skFitSpline(sketch, "E43", {"points": [v(-15.5, -10.33) * mm, v(-12.3, -10.33) * mm, v(-9.53, -11.4) * mm, v(-9.8, -13.31) * mm, v(-15.5, -13.21) * mm], "startDerivative": vector(12.6, 0.65) * mm, "endDerivative": vector(-21.77, 3.79) * mm});
            skSolve(sketch);
        }
        {
            var Q0;
            {var subQ0=sQuery(id+"F25.wireOp",EDGE,"E43");var subQ1=makeQuery(id+"F7.opExtrude","CAP_EDGE",EDGE,{"disambiguationData":[OSD([sQuery(id+"F6.wireOp",EDGE,"E7.left")])],"isStart":false});var subQ2=makeQuery(id+"F25.imprint","INTERSECT",VERTEX,{"disambiguationData":[OD(0.0)],"derivedFrom":[subQ1,subQ0]});Q0=makeQuery(id+"F25.imprint","IMPRINT",FACE,{"disambiguationData":[TD([[makeQuery(id+"F25.imprint","IMPRINT",EDGE,{"disambiguationData":[TD([[subQ2,1.0]])],"derivedFrom":subQ0}),-1.0]])]});}
            var Q1;
            Q1=makeQuery(id+"F1.opExtrude","SWEPT_FACE",FACE,{"disambiguationData":[OSD([sQuery(id+"F0.wireOp",EDGE,"E0.left")])]});
            var Q2;
            {var subQ0=sQuery(id+"F2.wireOp",EDGE,"E2.left");Q2=makeQuery(id+"F5.boolean.opBoolean","COPY",FACE,{"derivedFrom":makeQuery(id+"F5.opExtrude","SWEPT_FACE",FACE,{"disambiguationData":[OSD([subQ0]),TDD([makeQuery(id+"F2.imprint","IMPRINT",EDGE,{"disambiguationData":[TD([[makeQuery(id+"F2.imprint","INTERSECT",VERTEX,{"derivedFrom":[subQ0,sQuery(id+"F2.wireOp",EDGE,"E3.top")]}),-1.0]])],"derivedFrom":subQ0})])]})});}
            extrude(context, id + "F26", {"entities" : qUnion([Q0, Q1, Q2]), "operationType" : NewBodyOperationType.REMOVE, "oppositeDirection" : true, "depth" : 0.5 * mm});
        }
    });
